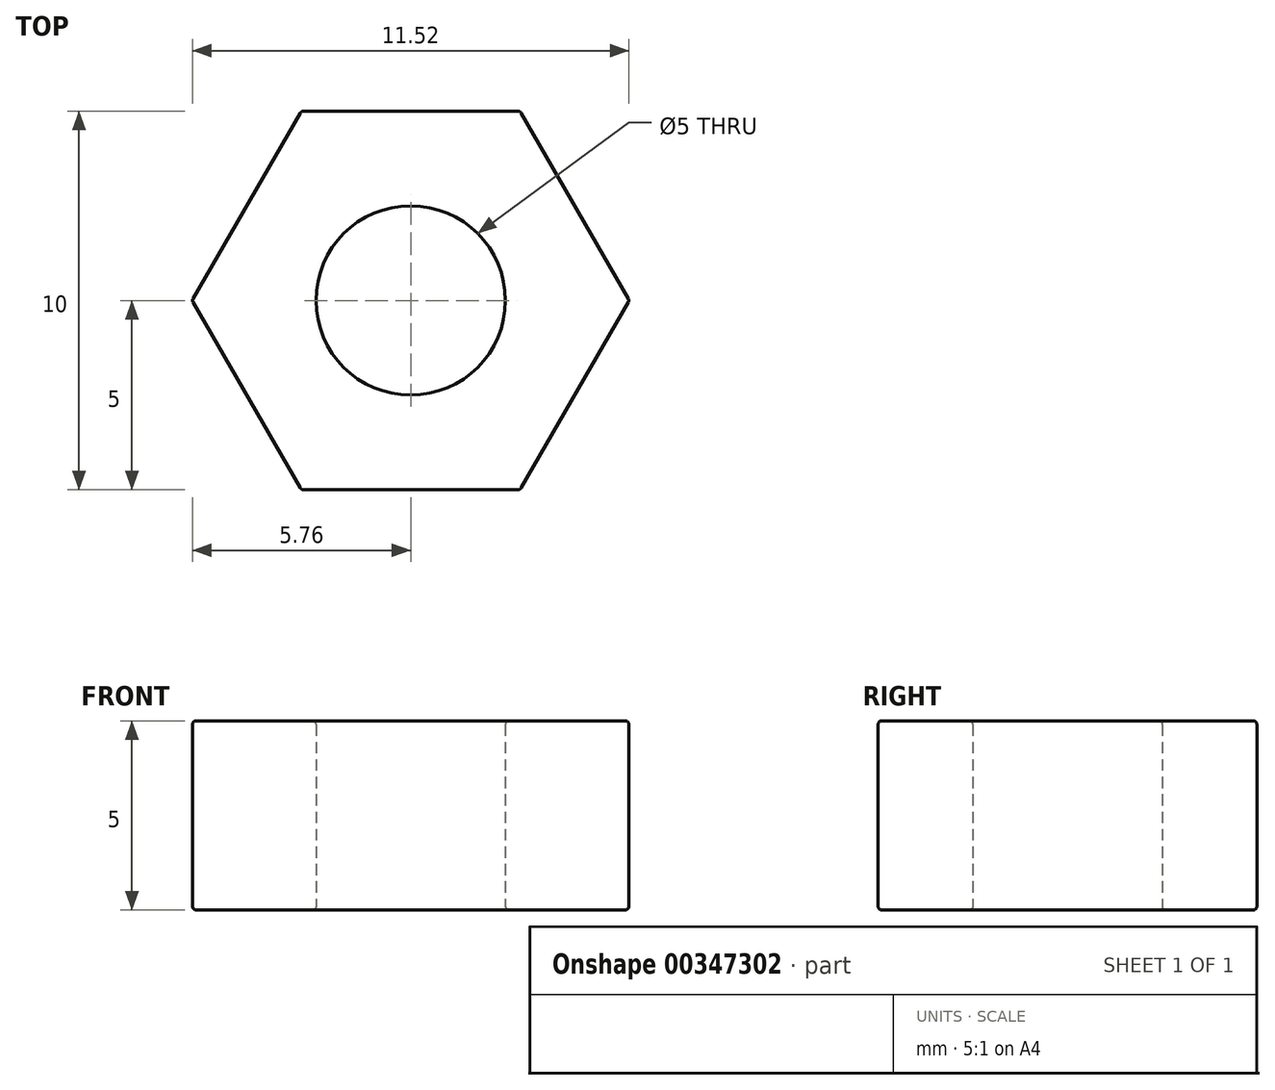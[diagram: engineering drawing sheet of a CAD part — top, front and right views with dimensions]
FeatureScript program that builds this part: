
annotation { "Feature Type Name" : "Feature", "Feature Type Description" : "" }
export const myFeature = defineFeature(function(context is Context, id is Id, definition is map)
    precondition{}
    {
        {
            var Q0;
            Q0=qCreatedBy(makeId("Top.planeOp"),FACE);
            var sketch = newSketch(context, id + "F0", { "sketchPlane" : qUnion([Q0])});
            skCircle(sketch, "E0.cCircle", {"center": v(0, 0) * mm, "radius": 5 * mm, "construction": true});
            skLineSegment(sketch, "E0.0", {"start": v(2.89, -5) * mm, "end": v(-2.89, -5) * mm});
            skLineSegment(sketch, "E0.1", {"start": v(-2.89, -5) * mm, "end": v(-5.77, 0) * mm});
            skLineSegment(sketch, "E0.2", {"start": v(-5.77, 0) * mm, "end": v(-2.89, 5) * mm});
            skLineSegment(sketch, "E0.3", {"start": v(-2.89, 5) * mm, "end": v(2.89, 5) * mm});
            skLineSegment(sketch, "E0.4", {"start": v(2.89, 5) * mm, "end": v(5.77, 0) * mm});
            skLineSegment(sketch, "E0.5", {"start": v(5.77, 0) * mm, "end": v(2.89, -5) * mm});
            skPoint(sketch, "E0.0.midPoint", {"position": v(0, -5) * mm});
            skCircle(sketch, "E1", {"center": v(0, 0) * mm, "radius": 2.5 * mm});
            skSolve(sketch);
        }
        {
            var Q0;
            Q0 = qSketchRegion(id + "F0", true);
            extrude(context, id + "F1", {"entities" : qUnion([Q0]), "depth" : 5 * mm});
        }
        {
            var Q0;
            Q0=makeQuery(id+"F1.opExtrude","CAP_EDGE",EDGE,{"disambiguationData":[OSD([sQuery(id+"F0.wireOp",EDGE,"E0.0")])],"isStart":false});
            var Q1;
            Q1=makeQuery(id+"F1.opExtrude","CAP_EDGE",EDGE,{"disambiguationData":[OSD([sQuery(id+"F0.wireOp",EDGE,"E0.5")])],"isStart":false});
            var Q2;
            Q2=makeQuery(id+"F1.opExtrude","CAP_FACE",FACE,{"disambiguationData":[OSD([sQuery(id+"F0.wireOp",EDGE,"E0.0"),sQuery(id+"F0.wireOp",EDGE,"E0.1"),sQuery(id+"F0.wireOp",EDGE,"E0.2"),sQuery(id+"F0.wireOp",EDGE,"E0.3"),sQuery(id+"F0.wireOp",EDGE,"E0.4"),sQuery(id+"F0.wireOp",EDGE,"E0.5"),sQuery(id+"F0.wireOp",EDGE,"E1")])],"isStart":false});
            var Q3;
            Q3=makeQuery(id+"F1.opExtrude","CAP_EDGE",EDGE,{"disambiguationData":[OSD([sQuery(id+"F0.wireOp",EDGE,"E1")])],"isStart":false});
            var Q4;
            Q4=makeQuery(id+"F1.opExtrude","CAP_EDGE",EDGE,{"disambiguationData":[OSD([sQuery(id+"F0.wireOp",EDGE,"E1")])],"isStart":true});
            var Q5;
            Q5=makeQuery(id+"F1.opExtrude","CAP_EDGE",EDGE,{"disambiguationData":[OSD([sQuery(id+"F0.wireOp",EDGE,"E0.3")])],"isStart":true});
            var Q6;
            Q6=makeQuery(id+"F1.opExtrude","SWEPT_FACE",FACE,{"disambiguationData":[OSD([sQuery(id+"F0.wireOp",EDGE,"E0.2")])]});
            var Q7;
            Q7=makeQuery(id+"F1.opExtrude","SWEPT_FACE",FACE,{"disambiguationData":[OSD([sQuery(id+"F0.wireOp",EDGE,"E0.3")])]});
            var Q8;
            Q8=makeQuery(id+"F1.opExtrude","SWEPT_FACE",FACE,{"disambiguationData":[OSD([sQuery(id+"F0.wireOp",EDGE,"E0.4")])]});
            fillet(context, id + "F2", {"entities" : qUnion([Q0, Q1, Q2, Q3, Q4, Q5, Q6, Q7, Q8]), "radius" : 0.1 * mm, "tangentPropagation" : true, "allowEdgeOverflow" : false});
        }
        {
            var Q0;
            Q0=makeQuery(id+"F1.opExtrude","SWEPT_FACE",FACE,{"disambiguationData":[OSD([sQuery(id+"F0.wireOp",EDGE,"E0.0")])]});
            var Q1;
            Q1=makeQuery(id+"F1.opExtrude","SWEPT_FACE",FACE,{"disambiguationData":[OSD([sQuery(id+"F0.wireOp",EDGE,"E0.5")])]});
            var Q2;
            Q2=makeQuery(id+"F1.opExtrude","SWEPT_FACE",FACE,{"disambiguationData":[OSD([sQuery(id+"F0.wireOp",EDGE,"E0.1")])]});
            var Q3;
            Q3=makeQuery(id+"F1.opExtrude","CAP_FACE",FACE,{"disambiguationData":[OSD([sQuery(id+"F0.wireOp",EDGE,"E0.0"),sQuery(id+"F0.wireOp",EDGE,"E0.1"),sQuery(id+"F0.wireOp",EDGE,"E0.2"),sQuery(id+"F0.wireOp",EDGE,"E0.3"),sQuery(id+"F0.wireOp",EDGE,"E0.4"),sQuery(id+"F0.wireOp",EDGE,"E0.5"),sQuery(id+"F0.wireOp",EDGE,"E1")])],"isStart":false});
            var Q4;
            Q4=makeQuery(id+"F1.opExtrude","CAP_FACE",FACE,{"disambiguationData":[OSD([sQuery(id+"F0.wireOp",EDGE,"E0.0"),sQuery(id+"F0.wireOp",EDGE,"E0.1"),sQuery(id+"F0.wireOp",EDGE,"E0.2"),sQuery(id+"F0.wireOp",EDGE,"E0.3"),sQuery(id+"F0.wireOp",EDGE,"E0.4"),sQuery(id+"F0.wireOp",EDGE,"E0.5"),sQuery(id+"F0.wireOp",EDGE,"E1")])],"isStart":true});
            fillet(context, id + "F3", {"entities" : qUnion([Q0, Q1, Q2, Q3, Q4]), "radius" : 0.1 * mm, "tangentPropagation" : true, "allowEdgeOverflow" : false});
        }
    });
